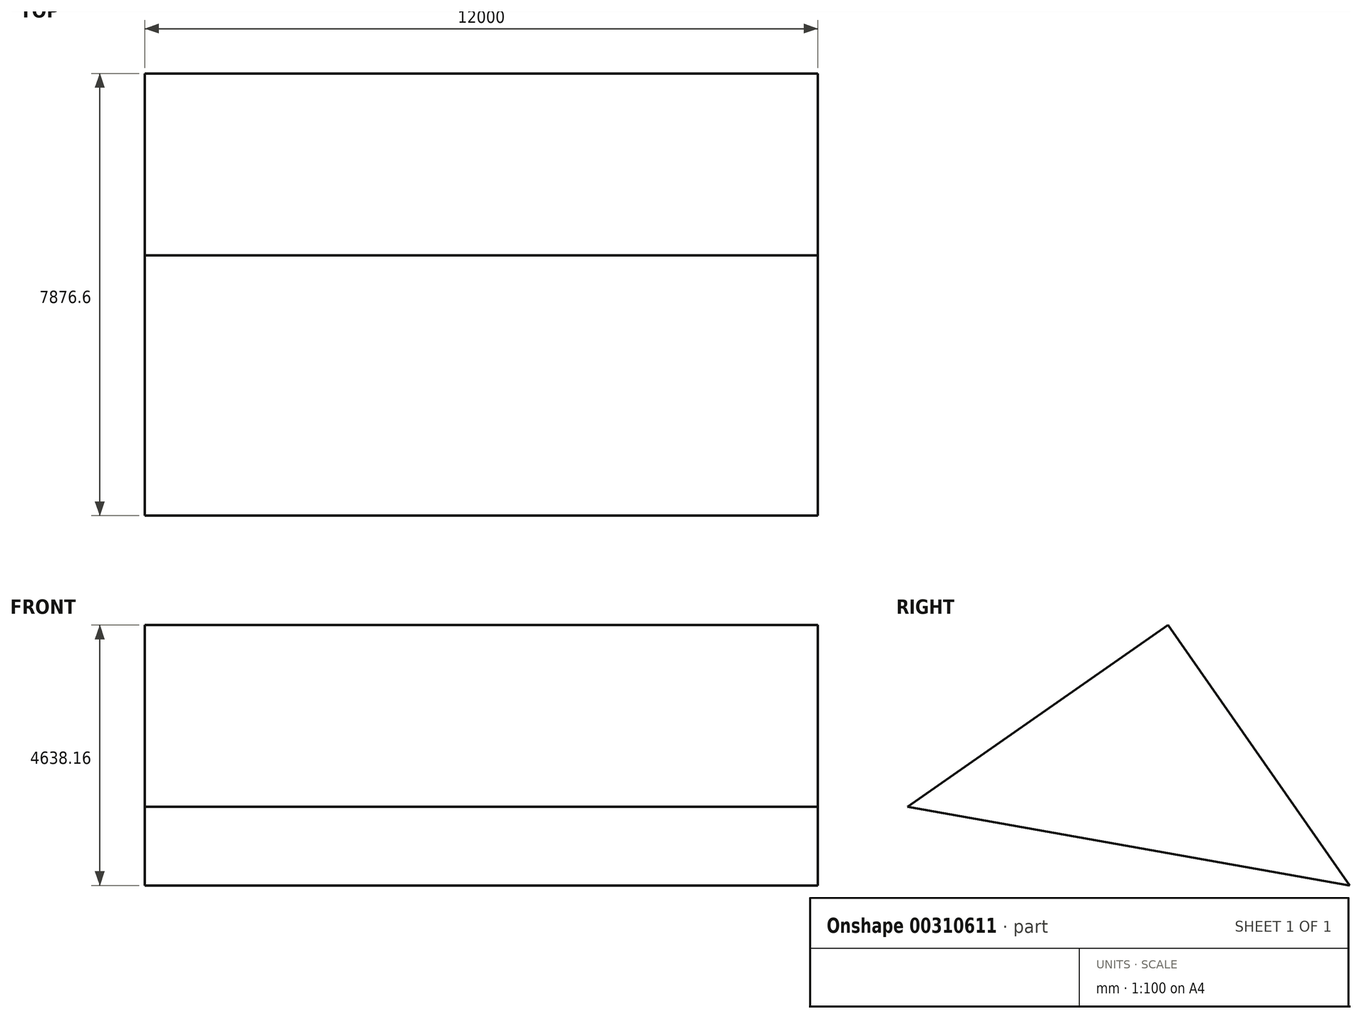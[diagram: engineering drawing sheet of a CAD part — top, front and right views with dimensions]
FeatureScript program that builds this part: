
annotation { "Feature Type Name" : "Feature", "Feature Type Description" : "" }
export const myFeature = defineFeature(function(context is Context, id is Id, definition is map)
    precondition{}
    {
        {
            var Q0;
            Q0=qCreatedBy(makeId("Right.planeOp"),FACE);
            var sketch = newSketch(context, id + "F0", { "sketchPlane" : qUnion([Q0])});
            skLineSegment(sketch, "E0", {"start": v(-3131.47, 0) * mm, "end": v(1506.7, 3238.42) * mm});
            skLineSegment(sketch, "E1", {"start": v(1506.7, 3238.42) * mm, "end": v(4745.13, -1399.74) * mm});
            skLineSegment(sketch, "E2", {"start": v(4745.13, -1399.74) * mm, "end": v(-3131.47, 0) * mm});
            skLineSegment(sketch, "E3", {"start": v(1506.7, 3238.42) * mm, "end": v(806.83, -699.87) * mm});
            skSolve(sketch);
        }
        {
            var Q0;
            Q0 = qSketchRegion(id + "F0", true);
            extrude(context, id + "F1", {"entities" : qUnion([Q0]), "depth" : 12000 * mm});
        }
    });
